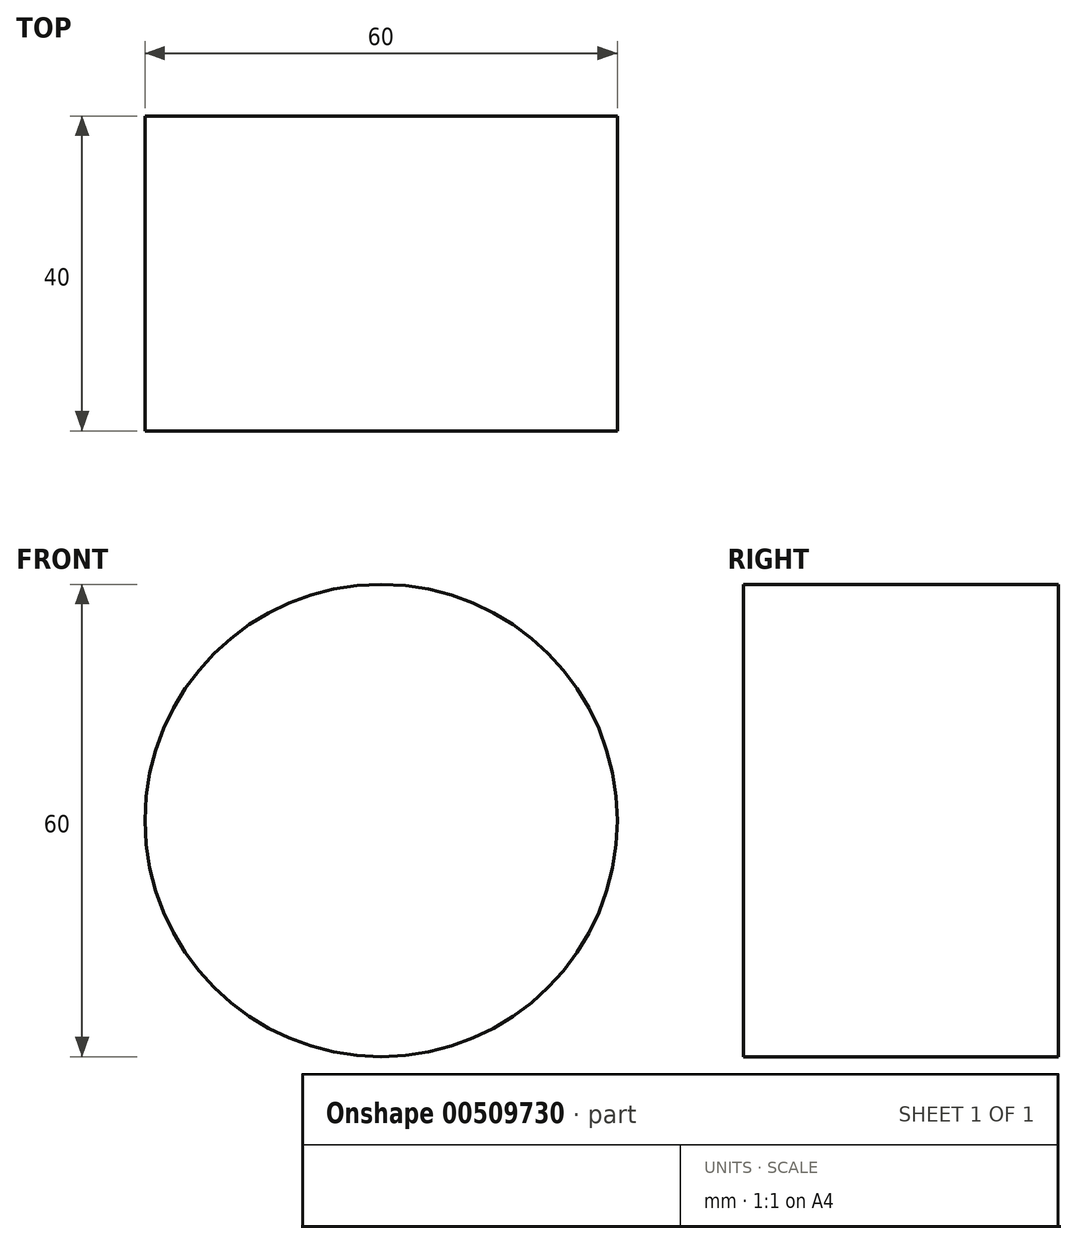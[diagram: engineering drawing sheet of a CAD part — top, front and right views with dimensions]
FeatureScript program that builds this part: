
annotation { "Feature Type Name" : "Feature", "Feature Type Description" : "" }
export const myFeature = defineFeature(function(context is Context, id is Id, definition is map)
    precondition{}
    {
        {
            var Q0;
            Q0=qCreatedBy(makeId("Front.planeOp"),FACE);
            var sketch = newSketch(context, id + "F0", { "sketchPlane" : qUnion([Q0])});
            skCircle(sketch, "E0", {"center": v(0, 0) * mm, "radius": 30 * mm});
            skSolve(sketch);
        }
        {
            var Q0;
            Q0 = qSketchRegion(id + "F0", true);
            extrude(context, id + "F1", {"entities" : qUnion([Q0]), "depth" : 40 * mm});
        }
    });
